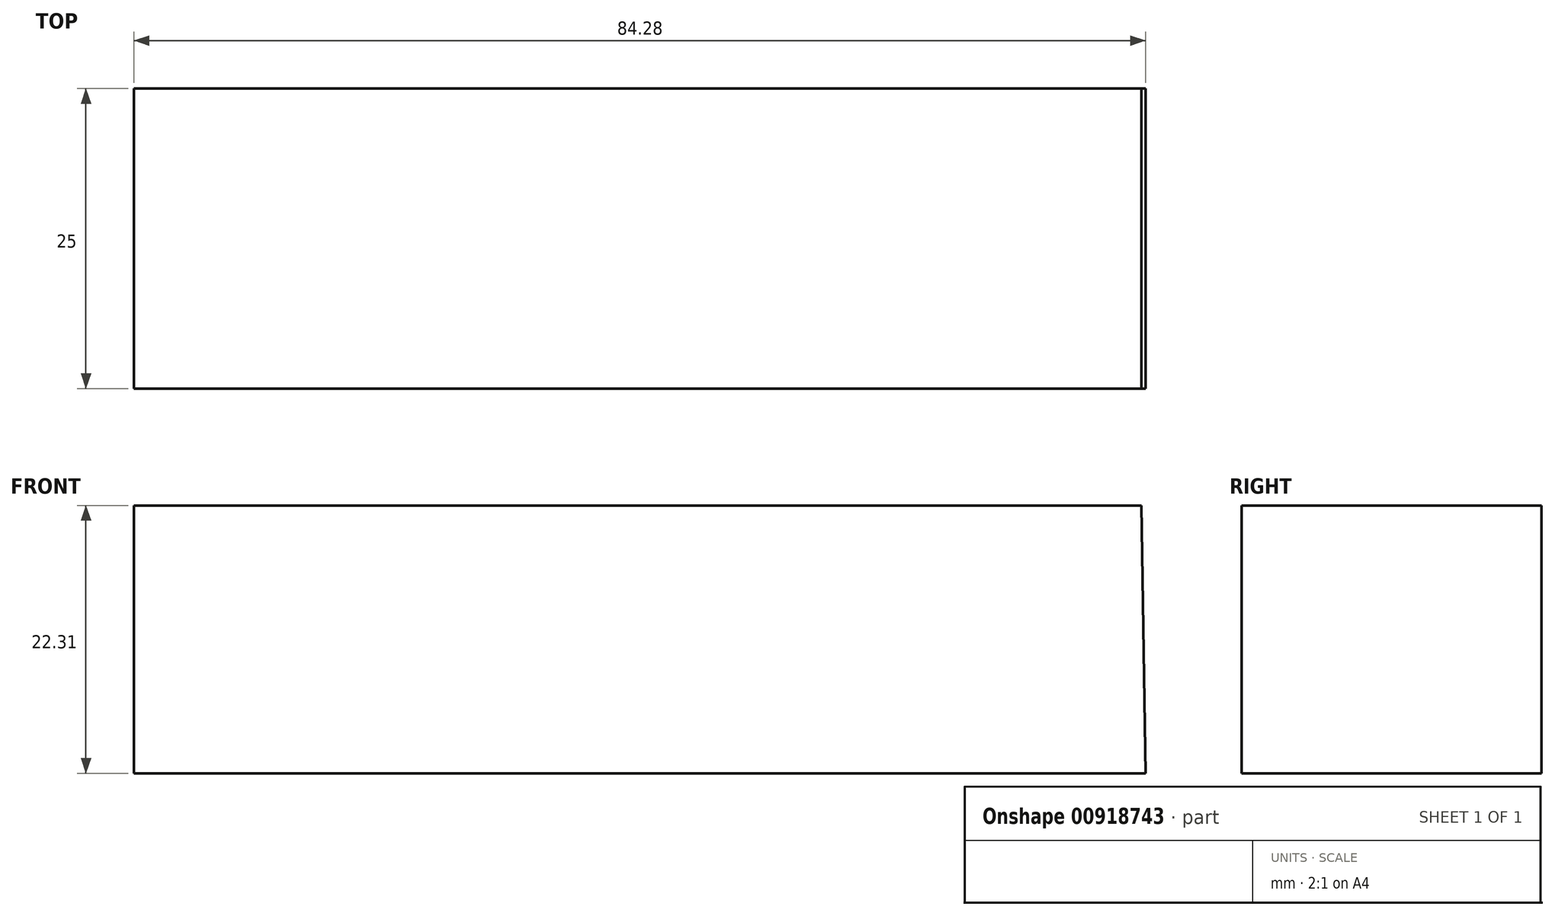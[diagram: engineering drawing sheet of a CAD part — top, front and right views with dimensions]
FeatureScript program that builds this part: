
annotation { "Feature Type Name" : "Feature", "Feature Type Description" : "" }
export const myFeature = defineFeature(function(context is Context, id is Id, definition is map)
    precondition{}
    {
        {
            var Q0;
            Q0=qCreatedBy(makeId("Front.planeOp"),FACE);
            var sketch = newSketch(context, id + "F0", { "sketchPlane" : qUnion([Q0])});
            skLineSegment(sketch, "E0", {"start": v(0, 0) * mm, "end": v(0, 36.29) * mm, "construction": true});
            skLineSegment(sketch, "E1", {"start": v(-39.82, 0) * mm, "end": v(44.46, 0) * mm});
            skLineSegment(sketch, "E2", {"start": v(-39.82, 0) * mm, "end": v(-39.82, 22.3) * mm});
            skLineSegment(sketch, "E3", {"start": v(-39.82, 22.3) * mm, "end": v(44.12, 22.3) * mm});
            skLineSegment(sketch, "E4", {"start": v(44.12, 22.3) * mm, "end": v(44.46, 0) * mm});
            skSolve(sketch);
        }
        {
            var Q0;
            Q0=makeQuery(id+"F0.imprint","IMPRINT",FACE,{"disambiguationData":[TD([[makeQuery(id+"F0.imprint","IMPRINT",EDGE,{"derivedFrom":sQuery(id+"F0.wireOp",EDGE,"E1")}),1.0]])]});
            extrude(context, id + "F1", {"entities" : qUnion([Q0]), "depth" : 25 * mm, "offsetDistance" : 25 * mm});
        }
    });
